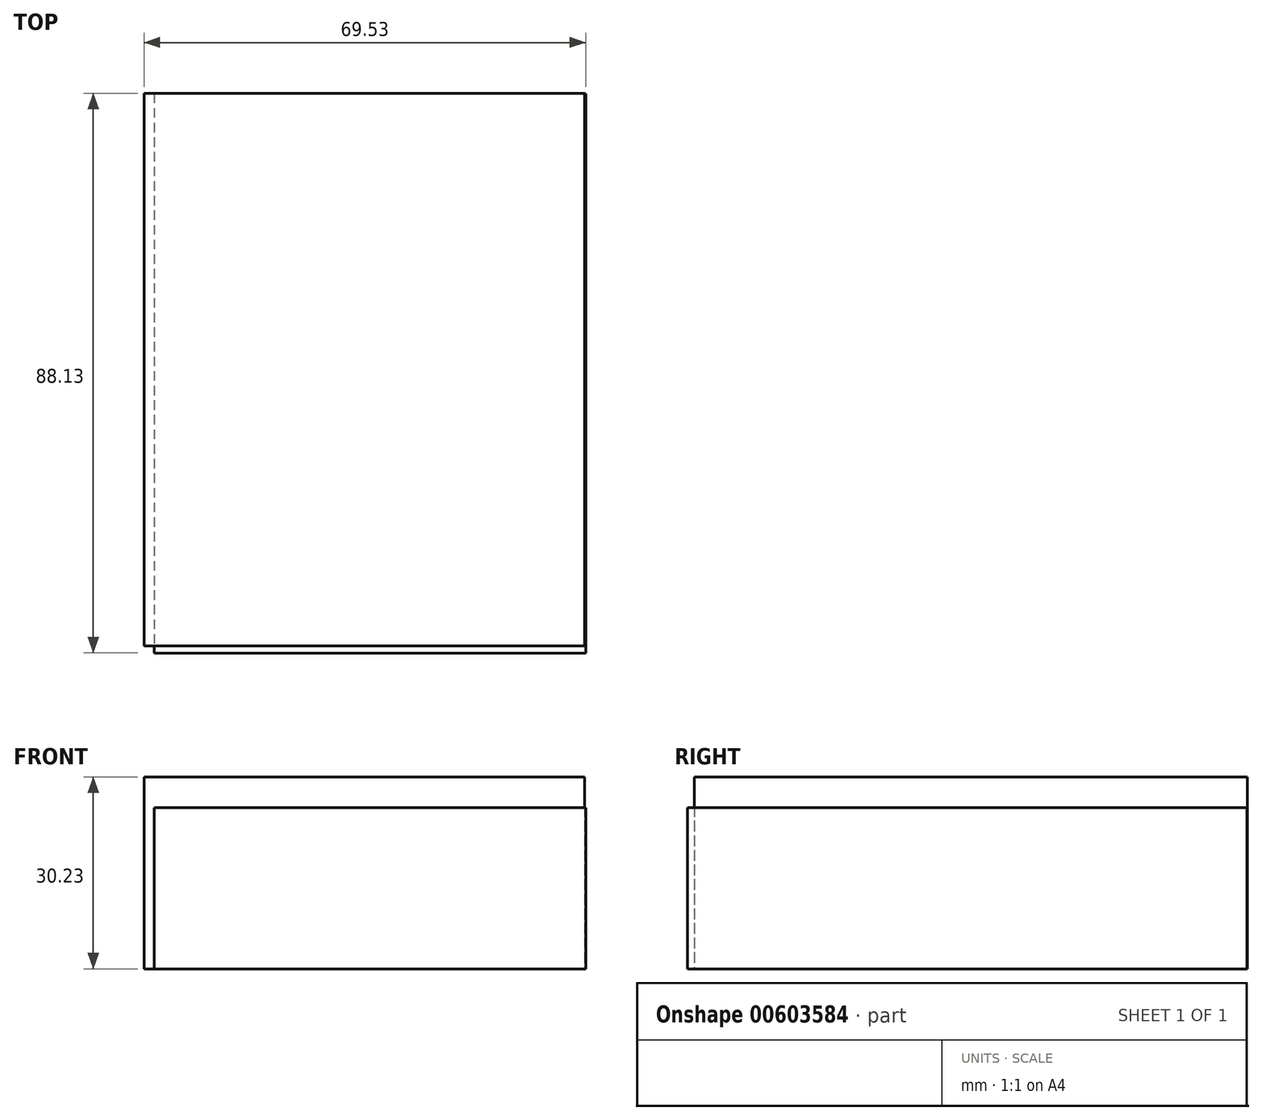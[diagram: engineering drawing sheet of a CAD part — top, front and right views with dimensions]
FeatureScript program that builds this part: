
annotation { "Feature Type Name" : "Feature", "Feature Type Description" : "" }
export const myFeature = defineFeature(function(context is Context, id is Id, definition is map)
    precondition{}
    {
        {
            var Q0;
            Q0=qCreatedBy(makeId("Top.planeOp"),FACE);
            var sketch = newSketch(context, id + "F0", { "sketchPlane" : qUnion([Q0])});
            skLineSegment(sketch, "E0.bottom", {"start": v(33.96, 44.03) * mm, "end": v(-33.96, 44.03) * mm});
            skLineSegment(sketch, "E0.top", {"start": v(33.96, -44.03) * mm, "end": v(-33.96, -44.03) * mm});
            skLineSegment(sketch, "E0.left", {"start": v(33.96, 44.03) * mm, "end": v(33.96, -44.03) * mm});
            skLineSegment(sketch, "E0.right", {"start": v(-33.96, 44.03) * mm, "end": v(-33.96, -44.03) * mm});
            skPoint(sketch, "E0.middle", {"position": v(0, 0) * mm});
            skSolve(sketch);
        }
        {
            var Q0;
            Q0=makeQuery(id+"F0.imprint","IMPRINT",FACE,{"disambiguationData":[TD([[makeQuery(id+"F0.imprint","IMPRINT",EDGE,{"derivedFrom":sQuery(id+"F0.wireOp",EDGE,"E0.bottom")}),1.0]])]});
            var sketch = newSketch(context, id + "F1", { "sketchPlane" : qUnion([Q0])});
            skLineSegment(sketch, "E1.bottom", {"start": v(-35.57, -42.93) * mm, "end": v(33.8, -42.93) * mm});
            skLineSegment(sketch, "E1.top", {"start": v(-35.57, 44.1) * mm, "end": v(33.8, 44.1) * mm});
            skLineSegment(sketch, "E1.left", {"start": v(-35.57, -42.93) * mm, "end": v(-35.57, 44.1) * mm});
            skLineSegment(sketch, "E1.right", {"start": v(33.8, -42.93) * mm, "end": v(33.8, 44.1) * mm});
            skSolve(sketch);
        }
        {
            var Q0;
            Q0 = qSketchRegion(id + "F1", true);
            extrude(context, id + "F2", {"entities" : qUnion([Q0]), "depth" : 30.23 * mm, "offsetDistance" : 25.4 * mm});
        }
        {
            var Q0;
            Q0=makeQuery(id+"F0.imprint","IMPRINT",FACE,{"disambiguationData":[TD([[makeQuery(id+"F0.imprint","IMPRINT",EDGE,{"derivedFrom":sQuery(id+"F0.wireOp",EDGE,"E0.bottom")}),1.0]])]});
            extrude(context, id + "F3", {"entities" : qUnion([Q0]), "depth" : 25.4 * mm});
        }
    });
